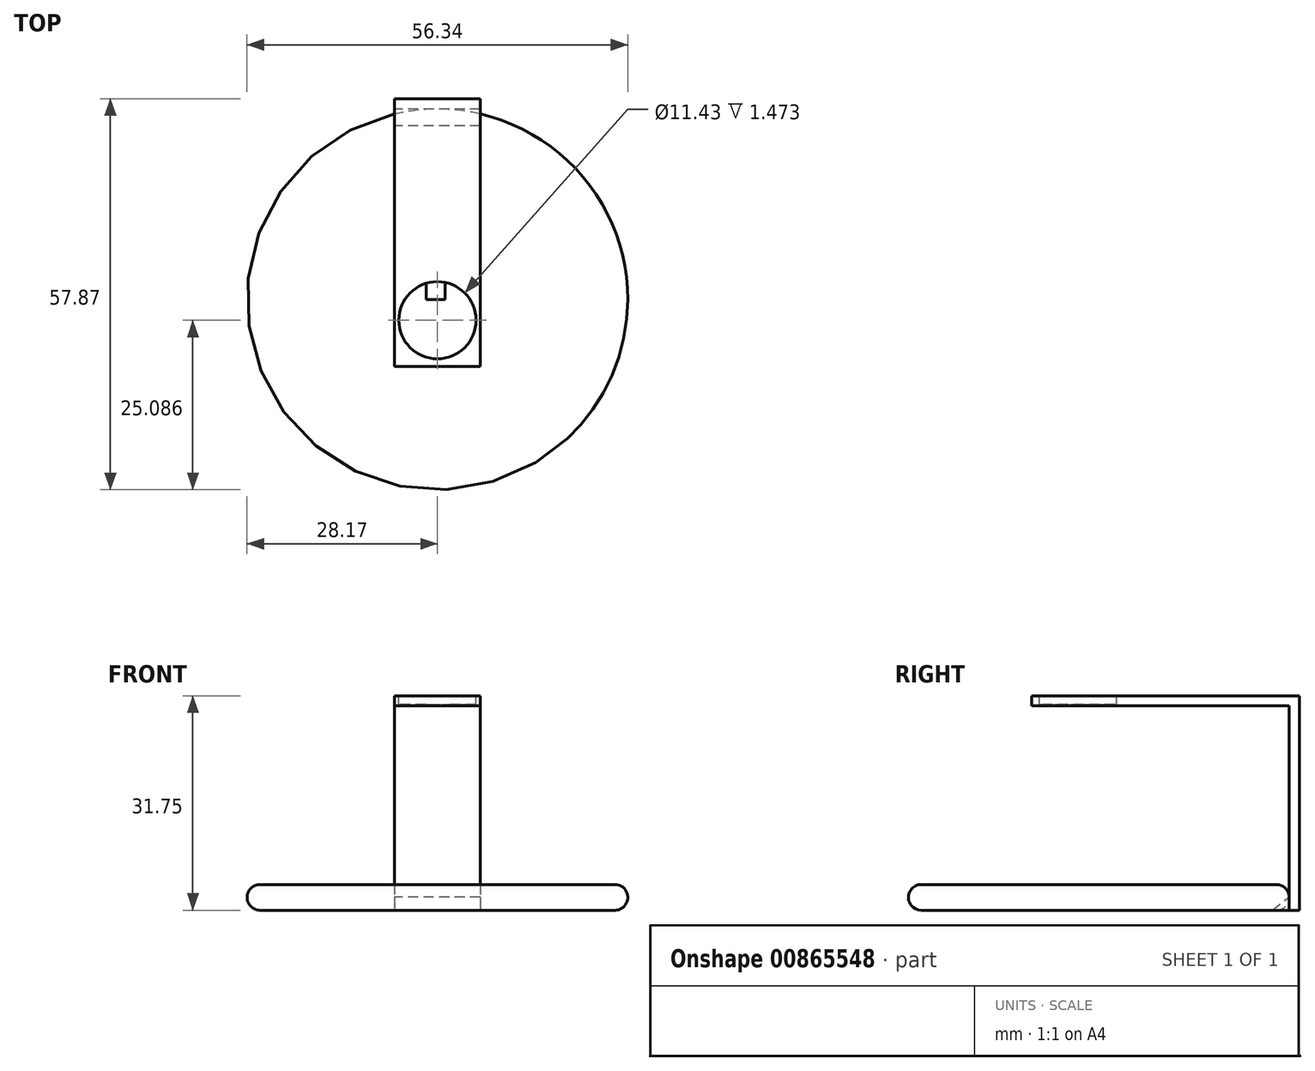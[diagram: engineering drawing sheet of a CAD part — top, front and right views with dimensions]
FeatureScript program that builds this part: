
annotation { "Feature Type Name" : "Feature", "Feature Type Description" : "" }
export const myFeature = defineFeature(function(context is Context, id is Id, definition is map)
    precondition{}
    {
        {
            var Q0;
            Q0=qCreatedBy(makeId("Top.planeOp"),FACE);
            var sketch = newSketch(context, id + "F0", { "sketchPlane" : qUnion([Q0])});
            skCircle(sketch, "E0", {"center": v(0, 0) * mm, "radius": 28.17 * mm});
            skSolve(sketch);
        }
        {
            var Q0;
            Q0 = qSketchRegion(id + "F0", true);
            extrude(context, id + "F1", {"entities" : qUnion([Q0]), "depth" : 3.8 * mm, "offsetDistance" : 25.4 * mm});
        }
        {
            var Q0;
            Q0=makeQuery(id+"F1.opExtrude","CAP_EDGE",EDGE,{"disambiguationData":[OSD([sQuery(id+"F0.wireOp",EDGE,"E0")])],"isStart":false});
            var Q1;
            Q1=makeQuery(id+"F1.opExtrude","CAP_EDGE",EDGE,{"disambiguationData":[OSD([sQuery(id+"F0.wireOp",EDGE,"E0")])],"isStart":true});
            fillet(context, id + "F2", {"entities" : qUnion([Q0, Q1]), "radius" : 1.9 * mm, "tangentPropagation" : true, "allowEdgeOverflow" : false});
        }
        {
            var Q0;
            Q0=makeQuery(id+"F1.opExtrude","CAP_FACE",FACE,{"disambiguationData":[OSD([sQuery(id+"F0.wireOp",EDGE,"E0")])],"isStart":true});
            var sketch = newSketch(context, id + "F3", { "sketchPlane" : qUnion([Q0])});
            skLineSegment(sketch, "E1", {"start": v(0, -28.18) * mm, "end": v(6.35, -28.18) * mm});
            skLineSegment(sketch, "E2", {"start": v(0, -28.18) * mm, "end": v(-6.35, -28.18) * mm});
            skLineSegment(sketch, "E3", {"start": v(-6.35, -28.18) * mm, "end": v(-6.35, -29.7) * mm});
            skLineSegment(sketch, "E4", {"start": v(-6.35, -29.7) * mm, "end": v(6.35, -29.7) * mm});
            skLineSegment(sketch, "E5", {"start": v(6.35, -29.7) * mm, "end": v(6.35, -28.18) * mm});
            skSolve(sketch);
        }
        {
            var Q0;
            Q0 = qSketchRegion(id + "F3", true);
            extrude(context, id + "F4", {"entities" : qUnion([Q0]), "oppositeDirection" : true, "depth" : 31.75 * mm, "offsetDistance" : 25.4 * mm});
        }
        {
            var Q0;
            Q0=makeQuery(id+"F4.opExtrude","SWEPT_FACE",FACE,{"disambiguationData":[OSD([sQuery(id+"F3.wireOp",EDGE,"E1"),sQuery(id+"F3.wireOp",EDGE,"E2")])]});
            var sketch = newSketch(context, id + "F5", { "sketchPlane" : qUnion([Q0])});
            skLineSegment(sketch, "E6", {"start": v(-6.35, 31.75) * mm, "end": v(6.35, 31.75) * mm});
            skLineSegment(sketch, "E7", {"start": v(6.35, 31.75) * mm, "end": v(6.35, 30.28) * mm});
            skLineSegment(sketch, "E8", {"start": v(6.35, 30.28) * mm, "end": v(-6.35, 30.28) * mm});
            skLineSegment(sketch, "E9", {"start": v(-6.35, 30.28) * mm, "end": v(-6.35, 31.75) * mm});
            skSolve(sketch);
        }
        {
            var Q0;
            Q0 = qSketchRegion(id + "F5", true);
            extrude(context, id + "F6", {"entities" : qUnion([Q0]), "operationType" : NewBodyOperationType.ADD, "depth" : 38.1 * mm, "offsetDistance" : 25.4 * mm});
        }
        {
            var Q0;
            Q0=makeQuery(id+"F6.boolean.opBoolean","MERGE",FACE,{"derivedFrom":[makeQuery(id+"F4.opExtrude","SWEPT_FACE",FACE,{"disambiguationData":[OSD([sQuery(id+"F3.wireOp",EDGE,"E3")])]}),makeQuery(id+"F6.opExtrude","SWEPT_FACE",FACE,{"disambiguationData":[OSD([sQuery(id+"F5.wireOp",EDGE,"E9")])]})]});
            var sketch = newSketch(context, id + "F7", { "sketchPlane" : qUnion([Q0])});
            skLineSegment(sketch, "E10", {"start": v(-28.18, 0) * mm, "end": v(-25.67, 0) * mm});
            skLineSegment(sketch, "E11", {"start": v(-25.67, 0) * mm, "end": v(-28.18, 1.94) * mm});
            skLineSegment(sketch, "E12", {"start": v(-28.18, 1.94) * mm, "end": v(-28.18, 0) * mm});
            skSolve(sketch);
        }
        {
            var Q0;
            Q0 = qSketchRegion(id + "F7", true);
            extrude(context, id + "F8", {"entities" : qUnion([Q0]), "oppositeDirection" : true, "depth" : 12.7 * mm, "offsetDistance" : 25.4 * mm});
        }
        {
            var Q0;
            Q0=makeQuery(id+"F6.boolean.opBoolean","MERGE",FACE,{"derivedFrom":[makeQuery(id+"F4.opExtrude","CAP_FACE",FACE,{"disambiguationData":[OSD([sQuery(id+"F3.wireOp",EDGE,"E1"),sQuery(id+"F3.wireOp",EDGE,"E2"),sQuery(id+"F3.wireOp",EDGE,"E3"),sQuery(id+"F3.wireOp",EDGE,"E4"),sQuery(id+"F3.wireOp",EDGE,"E5")])],"isStart":false}),makeQuery(id+"F6.opExtrude","SWEPT_FACE",FACE,{"disambiguationData":[OSD([sQuery(id+"F5.wireOp",EDGE,"E6")])]})]});
            var sketch = newSketch(context, id + "F9", { "sketchPlane" : qUnion([Q0])});
            skCircle(sketch, "E13", {"center": v(0, -3.08) * mm, "radius": 5.72 * mm});
            skSolve(sketch);
        }
        {
            var Q0;
            Q0 = qSketchRegion(id + "F9", true);
            extrude(context, id + "F10", {"entities" : qUnion([Q0]), "operationType" : NewBodyOperationType.REMOVE, "oppositeDirection" : true, "depth" : 1.27 * mm, "offsetDistance" : 25.4 * mm});
        }
        {
            var Q0;
            Q0=makeQuery(id+"F10.boolean.opBoolean","COPY",FACE,{"derivedFrom":makeQuery(id+"F10.opExtrude","CAP_FACE",FACE,{"disambiguationData":[OSD([sQuery(id+"F9.wireOp",EDGE,"E13")])],"isStart":false})});
            var sketch = newSketch(context, id + "F11", { "sketchPlane" : qUnion([Q0])});
            skLineSegment(sketch, "E14", {"start": v(-1.65, 2.39) * mm, "end": v(-1.65, 0) * mm});
            skLineSegment(sketch, "E15", {"start": v(-1.65, 0) * mm, "end": v(1.15, 0) * mm});
            skLineSegment(sketch, "E16", {"start": v(1.15, 0) * mm, "end": v(1.15, 2.51) * mm});
            skSolve(sketch);
        }
        {
            var Q0;
            {var subQ0=sQuery(id+"F11.wireOp",EDGE,"E14");Q0=makeQuery(id+"F11.imprint","IMPRINT",FACE,{"disambiguationData":[TD([[makeQuery(id+"F11.imprint","IMPRINT",EDGE,{"derivedFrom":subQ0}),1.0]])]});}
            extrude(context, id + "F12", {"entities" : qUnion([Q0]), "operationType" : NewBodyOperationType.REMOVE, "oppositeDirection" : true, "depth" : 25.4 * mm, "offsetDistance" : 25.4 * mm});
        }
    });
